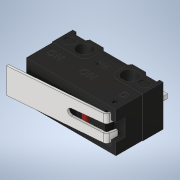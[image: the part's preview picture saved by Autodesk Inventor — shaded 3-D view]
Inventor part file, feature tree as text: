
AUTODESK INVENTOR PART (.ipt)
format: ipt  version: 2020.1 (Build 241239000, 239)  size: 1,119,232 bytes
history: native  units: mm
features: other x3, surface_op x1, extrude x1, sketch x1
ambient origin geometry x8: Origin, YZ Plane, XZ Plane, XY Plane, X Axis, Y Axis, Z Axis, Center Point
bodies: Solid1 (feature_tree), Solid2 (feature_tree)
feature tree (6):
  surface_op  "Sculpt1"
  extrude  "Extrusion1"  [1 undecoded]
  sketch  "Sketch2"  dims[d4=2.0mm d5=0.0mm]
  other  "ZMA00A150L04PC"
  other  "Composite1"
  other  "Srf1"
note: 1 required parameter value undecoded (feature->parameter linkage not recoverable at this tier; creation-order binding heuristic only, values carry confidence <= 0.55)
